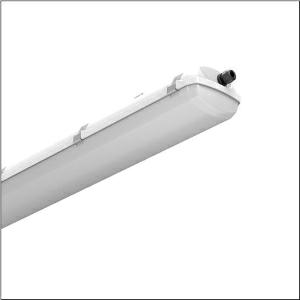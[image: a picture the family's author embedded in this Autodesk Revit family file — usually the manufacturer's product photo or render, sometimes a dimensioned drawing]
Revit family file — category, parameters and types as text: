
# Revit family: monsun_r__ex_51fxb2dl480a_525c
name_source: partatom
category: Lighting Fixtures
units: mm (PartAtom-declared; Revit-internal decimal feet)

## family parameters
Cut with Voids When Loaded = No
Host = Face
Light Source = No
Part Type = Normal
Room Calculation Point = No
Round Connector Dimension = Use Diameter
Shared = No

## types (1)
- Monsun® Ex (1 x LED, 8720 lm, 58.4 W, 4000K)
    Apparent Load = 58 VA
    CIE Flux Codes = 43 72 91 92 100
    Color Rendering = 80
    Color Temperature = 4000K
    Default Elevation = 1800 mm
    Description = Monsun® Ex, damp-proof luminaire, primary optical cover: cover, of PC, UV-stabilised, opal, light emission: direct distribution, primary light characteristic: symmetric, installation type: surface-mounted, LED, rated luminous flux: 8.720lm, luminous efficacy: 149lm/W, light colour: 840, colour temperature: 4000K, control gear: ECG DALI, with terminal, 5-pole, max. 2.5mm², through-wiring: 7x 2.5mm², mains connection: 220..240V, AC, 50/60Hz, rated input power: 58W, housing, of PC, light grey (RAL 7035), incl. blind plug, incl. 1x Ex cable gland M20 for cable diameter 7..12mm with sealing, length: 1.280mm, width: 155mm, height: 105mm, clip for enclosure, of stainless steel, protection rating (complete): IP66, insulation class (complete): insulation class I (protective earthing), certification: CE, explosion class: zone2,22 II 3G Ex nR IIC T6 GC, II 3D Ex tc IIIC T80°C Dc, impact resistance: IK10, permissible operating ambient temperature: -20..+60°C, LABS conformity tested according to VDMA 24364:2018-05, contact your sales advisor before using the luminaires in applications with unclear chemical exposure, large temperature fluctuations or condensation-forming humidity, packaging unit: 1 piece
    Height = 105 mm
    Lamp = 1 x LED
    Lamp Light Flux = 8720 lm
    Lamp Power = 58.4 W
    Lamp count = 1
    Length = 1280 mm
    Luminous efficacy = 149 lm/W
    Manufacturer = Siteco
    ModVariant = No
    Model = 51FXB2DL480A
    Mounting Place = Ceiling
    Mounting Type = Surface mounted
    Number of Poles = 1
    OnlyDefault = Yes
    Power Factor = 1
    Product Name = Monsun® Ex
    Product group = damp-proof luminaire
    ProductGroupID = 300
    Protection Class = Protection class I
    Protection Degree = IP 66
    RLX_Detail_Level = 1
    RLX_Emergency_Light_Flux = 0 lm
    RLX_Emergency_Type = 0
    RLX_Emergency_Type_DB = No
    RlxData = <blob elided: 41509 chars, md5=9b4fff1a>
    Socket = socket
    Standby Power = 0 W
    System Light Flux = 8720 lm
    System Power = 58 W
    Type Comments = Product without accessories
    Type Image = l_1258882.jpg
    URL = http://relux.com
    VarID = ---
    Voltage = 0 V
    Weight = 0.00 kg
    Width = 155 mm

## geometry (parser evidence)
native form markers: Blend x4, Sweep x12
no freeform markers — native parametric forms only
